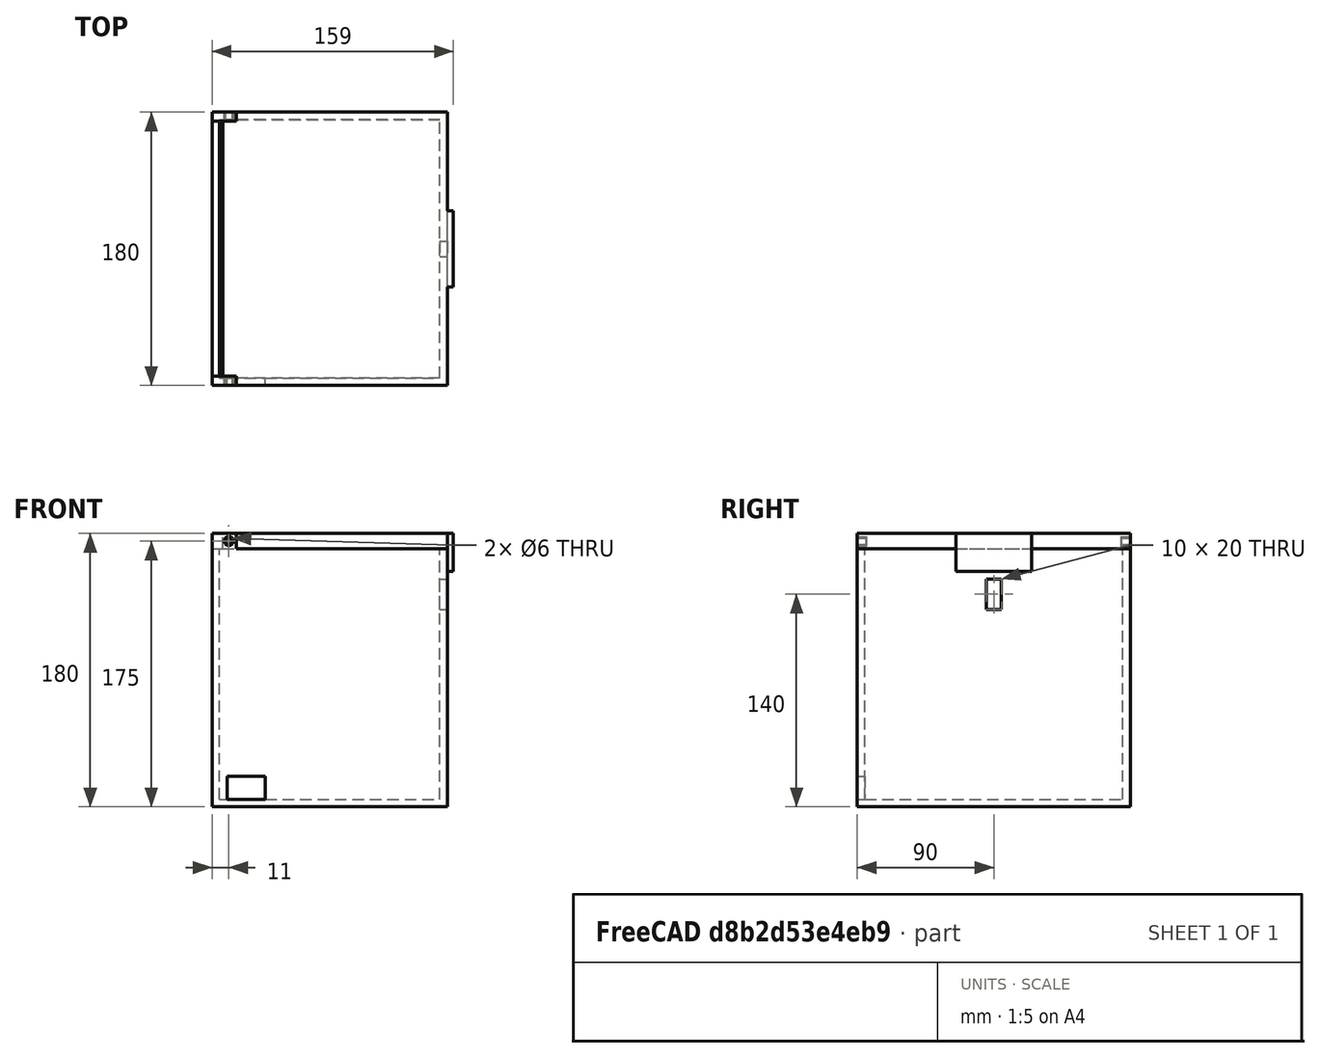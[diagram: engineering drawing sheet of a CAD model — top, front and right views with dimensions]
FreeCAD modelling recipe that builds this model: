
FCSTD DOCUMENT  (FreeCAD 1.0R38806 (Git))
Label: Caja_y tapa_arregladas
License: All rights reserved
LicenseURL: https://en.wikipedia.org/wiki/All_rights_reserved
objects: Part::Box×18, Part::Cut×16, Part::Fuse×8, Part::Cylinder×6, TechDraw::DrawProjGroupItem×3, TechDraw::DrawSVGTemplate×2, TechDraw::DrawPage×2, TechDraw::DrawProjGroup×1
note: 48 computed .brp shape members not serialized (recipe doc carries the construction recipe); baked Part::Feature solids carry a one-line shape summary decoded from their .brp

FEATURE [Part::Box] Box002  label="tapa"
  AttacherType = Attacher::AttachEngine3D
  Height = 10
  Length = 155
  Placement = pos=(0,0,170) rot=(0,0,1;0rad)
  Width = 180
FEATURE [Part::Box] Box  label="Cube"
  AttacherType = Attacher::AttachEngine3D
  Height = 170
  Length = 155
  Width = 180
FEATURE [Part::Box] Box001  label="Cube001"
  AttacherType = Attacher::AttachEngine3D
  Height = 200
  Length = 145
  Placement = pos=(5,5,5) rot=(0,0,1;0rad)
  Width = 170
FEATURE [Part::Cut] Cut  label="EStructura"
  Base = -> Box
  Refine = true
  Tool = -> Box001
FEATURE [Part::Box] Box003  label="Agujero"
  AttacherType = Attacher::AttachEngine3D
  Height = 15
  Length = 25
  Placement = pos=(10,-7,5) rot=(0,0,1;0rad)
  Width = 25
FEATURE [Part::Cut] Cut001  label="Caja_p1"
  Base = -> Cut
  Refine = true
  Tool = -> Box003
FEATURE [Part::Box] Box004  label="Cube002"
  AttacherType = Attacher::AttachEngine3D
  Height = 25
  Length = 4
  Placement = pos=(155,65,155) rot=(0,0,1;0rad)
  Width = 50
FEATURE [Part::Fuse] Fusion  label="tapa_sin_na"
  Base = -> Box002
  Refine = true
  Tool = -> Box004
FEATURE [Part::Box] Box005  label="Cube003"
  AttacherType = Attacher::AttachEngine3D
  Height = 20
  Length = 12
  Placement = pos=(146,85,130) rot=(0,0,1;0rad)
  Width = 10
FEATURE [Part::Cut] Cut002  label="Caja"
  Base = -> Cut001
  Refine = true
  Tool = -> Box005
FEATURE [Part::Box] Box006  label="visagra_1_1"
  AttacherType = Attacher::AttachEngine3D
  Height = 10
  Length = 16
  Placement = pos=(0,174,170) rot=(0,0,1;0rad)
  Width = 6
FEATURE [Part::Box] Box007  label="visagra2_1"
  AttacherType = Attacher::AttachEngine3D
  Height = 10
  Length = 16
  Placement = pos=(0,0,170) rot=(0,0,1;0rad)
  Width = 6
FEATURE [Part::Cylinder] Cylinder
  Angle = 360
  AttacherType = Attacher::AttachEngine3D
  FirstAngle = 0
  Height = 148
  Placement = pos=(7,192,175) rot=(1,0,0;1.5708rad)
  Radius = 3
  SecondAngle = 0
FEATURE [Part::Cut] Cut003  label="visagra1"
  Base = -> Box006
  Refine = true
  Tool = -> Cylinder
FEATURE [Part::Cylinder] Cylinder001
  Angle = 360
  AttacherType = Attacher::AttachEngine3D
  FirstAngle = 0
  Height = 148
  Placement = pos=(7,139,175) rot=(1,0,0;1.5708rad)
  Radius = 3
  SecondAngle = 0
FEATURE [Part::Cut] Cut004  label="visagra2"
  Base = -> Box007
  Refine = true
  Tool = -> Cylinder001
FEATURE [Part::Fuse] Fusion001
  Base = -> Cut002
  Refine = true
  Tool = -> Cut003
FEATURE [Part::Fuse] Fusion002  label="cuerpo"
  Base = -> Fusion001
  Refine = true
  Tool = -> Cut004
FEATURE [Part::Cut] Cut005  label="Tapa"
  Base = -> Fusion
  Refine = true
  Tool = -> Fusion002
FEATURE [Part::Box] Box008  label="Cube004"
  AttacherType = Attacher::AttachEngine3D
  Height = 170
  Length = 155
  Width = 180
FEATURE [Part::Box] Box009  label="Cube005"
  AttacherType = Attacher::AttachEngine3D
  Height = 200
  Length = 145
  Placement = pos=(5,5,5) rot=(0,0,1;0rad)
  Width = 170
FEATURE [Part::Box] Box010  label="Agujero001"
  AttacherType = Attacher::AttachEngine3D
  Height = 15
  Length = 25
  Placement = pos=(10,-7,5) rot=(0,0,1;0rad)
  Width = 25
FEATURE [Part::Box] Box011  label="Cube006"
  AttacherType = Attacher::AttachEngine3D
  Height = 20
  Length = 12
  Placement = pos=(146,85,130) rot=(0,0,1;0rad)
  Width = 10
FEATURE [Part::Box] Box012  label="visagra_1_002"
  AttacherType = Attacher::AttachEngine3D
  Height = 10
  Length = 16
  Placement = pos=(0,174,170) rot=(0,0,1;0rad)
  Width = 6
FEATURE [Part::Box] Box013  label="visagra2_002"
  AttacherType = Attacher::AttachEngine3D
  Height = 10
  Length = 16
  Placement = pos=(0,0,170) rot=(0,0,1;0rad)
  Width = 6
FEATURE [Part::Cut] Cut006  label="EStructura001"
  Base = -> Box008
  Refine = true
  Tool = -> Box009
FEATURE [Part::Cut] Cut007  label="Caja_p002"
  Base = -> Cut006
  Refine = true
  Tool = -> Box010
FEATURE [Part::Cut] Cut008  label="Caja001"
  Base = -> Cut007
  Refine = true
  Tool = -> Box011
FEATURE [Part::Cylinder] Cylinder002
  Angle = 360
  AttacherType = Attacher::AttachEngine3D
  FirstAngle = 0
  Height = 148
  Placement = pos=(11,191,175) rot=(1,0,0;1.5708rad)
  Radius = 3
  SecondAngle = 0
FEATURE [Part::Cut] Cut009  label="visagra003"
  Base = -> Box012
  Refine = true
  Tool = -> Cylinder002
FEATURE [Part::Cylinder] Cylinder003
  Angle = 360
  AttacherType = Attacher::AttachEngine3D
  FirstAngle = 0
  Height = 148
  Placement = pos=(11,139,175) rot=(1,0,0;1.5708rad)
  Radius = 3
  SecondAngle = 0
FEATURE [Part::Cut] Cut010  label="visagra004"
  Base = -> Box013
  Refine = true
  Tool = -> Cylinder003
FEATURE [Part::Fuse] Fusion003
  Base = -> Cut008
  Refine = true
  Tool = -> Cut009
FEATURE [Part::Fuse] Fusion004  label="Caja002"
  Base = -> Fusion003
  Refine = true
  Tool = -> Cut010
FEATURE [Part::Box] Box014  label="Cube007"
  AttacherType = Attacher::AttachEngine3D
  Height = 10
  Length = 11
  Placement = pos=(-4,0,170) rot=(0,0,1;0rad)
  Width = 180
FEATURE [Part::Cut] Cut011
  Base = -> Cut005
  Refine = true
  Tool = -> Box014
FEATURE [Part::Box] Box015  label="Cube008"
  AttacherType = Attacher::AttachEngine3D
  Height = 10
  Length = 10
  Placement = pos=(2,174,170) rot=(0,0,1;0rad)
  Width = 10
FEATURE [Part::Box] Box016  label="Cube009"
  AttacherType = Attacher::AttachEngine3D
  Height = 10
  Length = 10
  Placement = pos=(2,-4,170) rot=(0,0,1;0rad)
  Width = 10
FEATURE [Part::Cut] Cut012
  Base = -> Cut011
  Refine = true
  Tool = -> Box016
FEATURE [Part::Cut] Cut013
  Base = -> Cut012
  Refine = true
  Tool = -> Box015
FEATURE [Part::Box] Box017  label="Cube010"
  AttacherType = Attacher::AttachEngine3D
  Height = 10
  Length = 10
  Placement = pos=(7,0,170) rot=(0,0,1;0rad)
  Width = 180
FEATURE [Part::Fuse] Fusion005
  Base = -> Cut013
  Refine = true
  Tool = -> Box017
FEATURE [Part::Cylinder] Cylinder004
  Angle = 360
  AttacherType = Attacher::AttachEngine3D
  FirstAngle = 0
  Height = 139
  Placement = pos=(11,139,175) rot=(1,0,0;1.5708rad)
  Radius = 2
  SecondAngle = 0
FEATURE [Part::Cylinder] Cylinder005
  Angle = 360
  AttacherType = Attacher::AttachEngine3D
  FirstAngle = 0
  Height = 137
  Placement = pos=(11,180,175) rot=(1,0,0;1.5708rad)
  Radius = 2
  SecondAngle = 0
FEATURE [Part::Cut] Cut014
  Base = -> Fusion005
  Refine = true
  Tool = -> Box012
FEATURE [Part::Cut] Cut015
  Base = -> Cut014
  Refine = true
  Tool = -> Box013
FEATURE [Part::Fuse] Fusion006
  Base = -> Cut015
  Refine = true
  Tool = -> Cylinder004
FEATURE [Part::Fuse] Fusion007  label="Tapa001"
  Base = -> Fusion006
  Refine = true
  Tool = -> Cylinder005
FEATURE [TechDraw::DrawSVGTemplate] Template
  EditableTexts = AuthorName=Eva Fernández de la Cruz; CheckDate=14/11/2024; CreationDate=11/14/24; DrawingNumber=NUMBER; FC-Scale=Automatic; FC-Title=Caja_arreglada; SheetNumber=1 / 1; Subtitle=SUBTITLE; Weight=WEIGHT
  Height = 297
  Orientation = 1
  Template = <path>
  Width = 420
FEATURE [TechDraw::DrawSVGTemplate] Template001
  EditableTexts = AuthorName=Eva Fernández de la Cruz; CheckDate=14/11/2024; CreationDate=11/14/24; DrawingNumber=NUMBER; FC-Scale=1 : 1; FC-Title=Tapa_arreglada; SheetNumber=1 / 1; Subtitle=SUBTITLE; Weight=WEIGHT
  Height = 297
  Orientation = 1
  Template = <path>
  Width = 420
FEATURE [TechDraw::DrawPage] Page001
  KeepUpdated = true
  NextBalloonIndex = 1
  ProjectionType = 0
  Template = -> Template001
FEATURE [TechDraw::DrawProjGroupItem] View  label="Front"
  CoarseView = false
  Direction = (0,-1,0)
  Focus = 100
  HardHidden = false
  IsoCount = 0
  IsoHidden = false
  IsoVisible = false
  LockPosition = true
  Perspective = false
  Rotation = 0
  RotationVector = (1,0,0)
  Scale = 0.5
  ScaleType = 2
  ScrubCount = 1
  SeamHidden = false
  SeamVisible = false
  SmoothHidden = false
  SmoothVisible = true
  Source = -> [Fusion004]
  Type = 0
  X = 0
  XDirection = (1,0,0)
  Y = 0
FEATURE [TechDraw::DrawProjGroupItem] ProjItem001  label="Right"
  CoarseView = false
  Direction = (1,-1e-16,0)
  Focus = 100
  HardHidden = false
  IsoCount = 0
  IsoHidden = false
  IsoVisible = false
  LockPosition = false
  Perspective = false
  Rotation = 0
  RotationVector = (1,0,0)
  Scale = 0.5
  ScaleType = 0
  ScrubCount = 1
  SeamHidden = false
  SeamVisible = false
  SmoothHidden = false
  SmoothVisible = true
  Source = -> [Fusion004]
  Type = 2
  X = -98.75
  XDirection = (1e-16,1,0)
  Y = 0
FEATURE [TechDraw::DrawProjGroupItem] ProjItem002  label="Top"
  CoarseView = false
  Direction = (0,0,1)
  Focus = 100
  HardHidden = false
  IsoCount = 0
  IsoHidden = false
  IsoVisible = false
  LockPosition = false
  Perspective = false
  Rotation = 0
  RotationVector = (1,0,0)
  ScaleType = 0
  ScrubCount = 1
  SeamHidden = false
  SeamVisible = false
  SmoothHidden = false
  SmoothVisible = true
  Source = -> [Fusion004]
  Type = 4
  X = 0
  XDirection = (1,0,0)
  Y = -105
FEATURE [TechDraw::DrawProjGroup] ProjGroup
  Anchor = -> View
  AutoDistribute = true
  LockPosition = false
  ProjectionType = 0
  Rotation = 0
  Scale = 0.5
  ScaleType = 1
  Source = -> [Fusion004]
  Views = -> [View,ProjItem001,ProjItem002]
  X = 166.876
  Y = 199.674
  spacingX = 15
  spacingY = 15
FEATURE [TechDraw::DrawPage] Page
  KeepUpdated = true
  NextBalloonIndex = 1
  ProjectionType = 0
  Template = -> Template
  Views = -> [ProjGroup]
note: 2 file-system paths scrubbed to <path> (originals preserved in the JSON sidecar)
